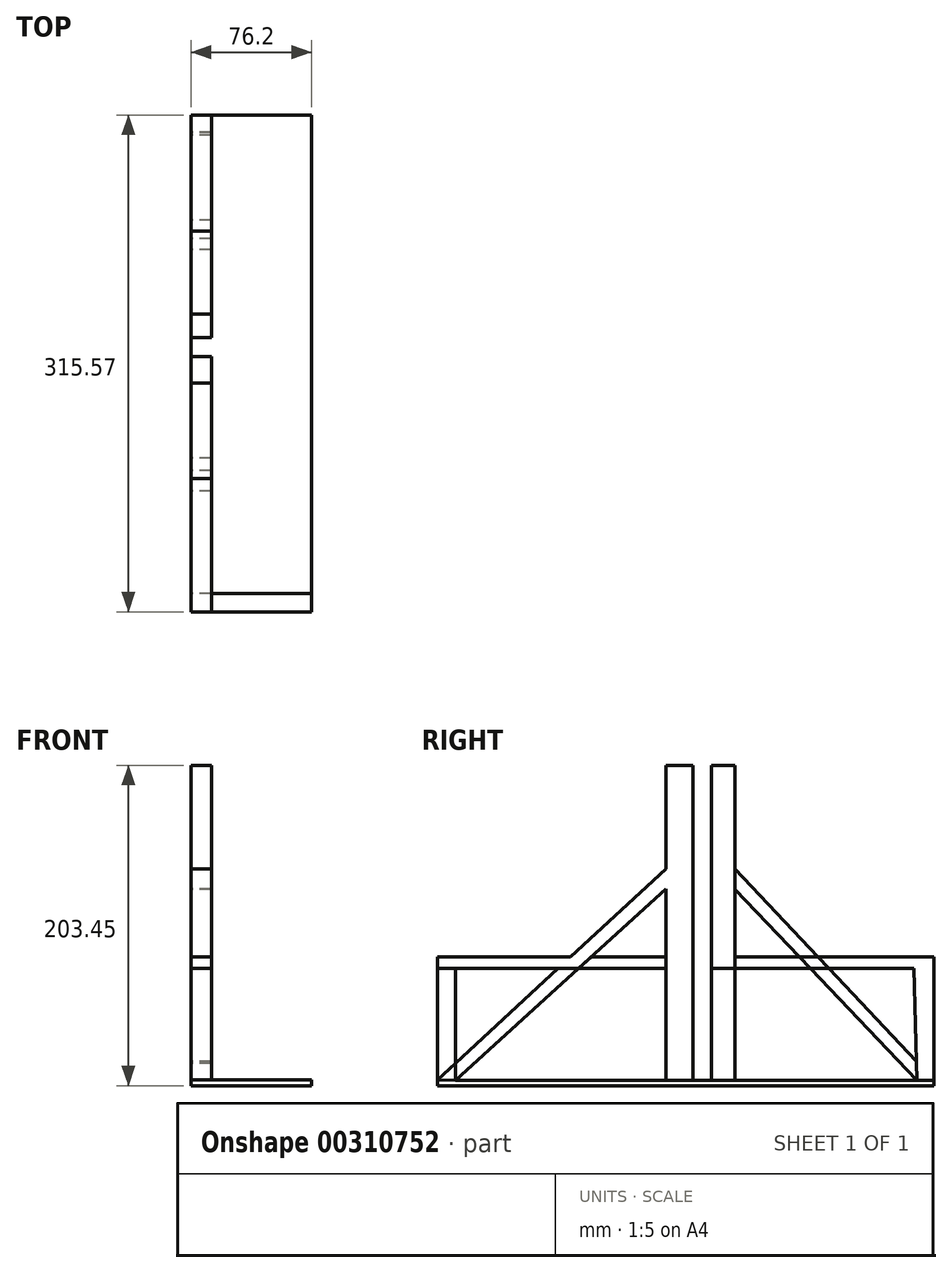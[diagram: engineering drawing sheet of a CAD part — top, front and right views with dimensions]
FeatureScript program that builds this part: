
annotation { "Feature Type Name" : "Feature", "Feature Type Description" : "" }
export const myFeature = defineFeature(function(context is Context, id is Id, definition is map)
    precondition{}
    {
        {
            var Q0;
            Q0=qCreatedBy(makeId("Right.planeOp"),FACE);
            var sketch = newSketch(context, id + "F0", { "sketchPlane" : qUnion([Q0])});
            skLineSegment(sketch, "E0.bottom", {"start": v(178.4, 15.69) * mm, "end": v(-125.56, 15.69) * mm});
            skLineSegment(sketch, "E0.top", {"start": v(178.4, -55.38) * mm, "end": v(-125.56, -55.38) * mm});
            skLineSegment(sketch, "E0.left", {"start": v(178.4, 15.69) * mm, "end": v(178.4, -55.38) * mm});
            skLineSegment(sketch, "E0.right", {"start": v(-125.56, 15.69) * mm, "end": v(-125.56, -55.38) * mm});
            skLineSegment(sketch, "E1", {"start": v(51.97, -55.38) * mm, "end": v(51.97, 144.7) * mm});
            skLineSegment(sketch, "E2", {"start": v(8.17, -55.38) * mm, "end": v(8.17, 144.7) * mm});
            skLineSegment(sketch, "E3", {"start": v(51.97, 144.7) * mm, "end": v(37.04, 144.7) * mm});
            skLineSegment(sketch, "E4", {"start": v(37.04, 144.7) * mm, "end": v(37.04, -55.38) * mm});
            skLineSegment(sketch, "E5", {"start": v(8.17, 144.7) * mm, "end": v(25.1, 144.7) * mm});
            skLineSegment(sketch, "E6", {"start": v(25.1, 144.7) * mm, "end": v(25.1, -55.38) * mm});
            skLineSegment(sketch, "E7", {"start": v(51.97, 79) * mm, "end": v(178.4, -55.38) * mm});
            skLineSegment(sketch, "E8", {"start": v(51.97, 66.06) * mm, "end": v(167.44, -55.38) * mm});
            skLineSegment(sketch, "E9", {"start": v(-125.56, 15.69) * mm, "end": v(-137.17, 15.69) * mm});
            skLineSegment(sketch, "E10", {"start": v(-137.17, 15.69) * mm, "end": v(-137.17, -55.2) * mm});
            skLineSegment(sketch, "E11", {"start": v(-137.17, -55.2) * mm, "end": v(-125.56, -55.38) * mm});
            skLineSegment(sketch, "E12", {"start": v(-137.17, 15.69) * mm, "end": v(-137.17, 22.96) * mm});
            skLineSegment(sketch, "E13", {"start": v(-137.17, 22.96) * mm, "end": v(8.17, 22.96) * mm});
            skLineSegment(sketch, "E14", {"start": v(51.97, 22.96) * mm, "end": v(178.4, 22.96) * mm});
            skLineSegment(sketch, "E15", {"start": v(178.4, 22.96) * mm, "end": v(178.4, 15.69) * mm});
            skLineSegment(sketch, "E16", {"start": v(8.17, 66.1) * mm, "end": v(-125.56, -55.38) * mm});
            skLineSegment(sketch, "E17", {"start": v(8.17, 79) * mm, "end": v(-137.17, -55.2) * mm});
            skLineSegment(sketch, "E18", {"start": v(165.56, 15.69) * mm, "end": v(167.44, -55.38) * mm});
            skLineSegment(sketch, "E19", {"start": v(178.4, -55.38) * mm, "end": v(178.4, -58.74) * mm});
            skLineSegment(sketch, "E20", {"start": v(178.4, -58.74) * mm, "end": v(-137.17, -58.74) * mm});
            skLineSegment(sketch, "E21", {"start": v(-137.17, -55.2) * mm, "end": v(-137.17, -58.74) * mm});
            skSolve(sketch);
        }
        {
            var Q0;
            {var subQ0=sQuery(id+"F0.wireOp",EDGE,"E0.left");Q0=makeQuery(id+"F0.imprint","IMPRINT",FACE,{"disambiguationData":[TD([[makeQuery(id+"F0.imprint","IMPRINT",EDGE,{"derivedFrom":subQ0}),-1.0]])]});}
            var Q1;
            {var subQ0=sQuery(id+"F0.wireOp",EDGE,"E7");var subQ3=sQuery(id+"F0.wireOp",EDGE,"E18");var subQ5=makeQuery(id+"F0.imprint","INTERSECT",VERTEX,{"derivedFrom":[subQ0,subQ3]});Q1=makeQuery(id+"F0.imprint","IMPRINT",FACE,{"disambiguationData":[TD([[makeQuery(id+"F0.imprint","IMPRINT",EDGE,{"disambiguationData":[TD([[subQ5,-1.0]])],"derivedFrom":subQ3}),1.0]])]});}
            var Q2;
            {var subQ0=sQuery(id+"F0.wireOp",EDGE,"E15");Q2=makeQuery(id+"F0.imprint","IMPRINT",FACE,{"disambiguationData":[TD([[makeQuery(id+"F0.imprint","IMPRINT",EDGE,{"derivedFrom":subQ0}),-1.0]])]});}
            var Q3;
            {var subQ0=sQuery(id+"F0.wireOp",EDGE,"E8");var subQ1=sQuery(id+"F0.wireOp",EDGE,"E0.bottom");var subQ2=makeQuery(id+"F0.imprint","INTERSECT",VERTEX,{"derivedFrom":[subQ1,subQ0]});Q3=makeQuery(id+"F0.imprint","IMPRINT",FACE,{"disambiguationData":[TD([[makeQuery(id+"F0.imprint","IMPRINT",EDGE,{"disambiguationData":[TD([[subQ2,-1.0]])],"derivedFrom":subQ1}),-1.0]])]});}
            var Q4;
            {var subQ0=sQuery(id+"F0.wireOp",EDGE,"E7");var subQ1=sQuery(id+"F0.wireOp",EDGE,"E1");var subQ2=makeQuery(id+"F0.imprint","INTERSECT",VERTEX,{"derivedFrom":[subQ1,subQ0]});Q4=makeQuery(id+"F0.imprint","IMPRINT",FACE,{"disambiguationData":[TD([[makeQuery(id+"F0.imprint","IMPRINT",EDGE,{"disambiguationData":[TD([[subQ2,1.0]])],"derivedFrom":subQ1}),-1.0]])]});}
            var Q5;
            {var subQ0=sQuery(id+"F0.wireOp",EDGE,"E4");var subQ1=sQuery(id+"F0.wireOp",EDGE,"E0.bottom");var subQ2=makeQuery(id+"F0.imprint","INTERSECT",VERTEX,{"derivedFrom":[subQ1,subQ0]});Q5=makeQuery(id+"F0.imprint","IMPRINT",FACE,{"disambiguationData":[TD([[makeQuery(id+"F0.imprint","IMPRINT",EDGE,{"disambiguationData":[TD([[subQ2,1.0]])],"derivedFrom":subQ1}),1.0]])]});}
            var Q6;
            {var subQ0=sQuery(id+"F0.wireOp",EDGE,"E6");var subQ1=sQuery(id+"F0.wireOp",EDGE,"E0.bottom");var subQ2=makeQuery(id+"F0.imprint","INTERSECT",VERTEX,{"derivedFrom":[subQ1,subQ0]});Q6=makeQuery(id+"F0.imprint","IMPRINT",FACE,{"disambiguationData":[TD([[makeQuery(id+"F0.imprint","IMPRINT",EDGE,{"disambiguationData":[TD([[subQ2,-1.0]])],"derivedFrom":subQ1}),1.0]])]});}
            var Q7;
            {var subQ8=sQuery(id+"F0.wireOp",EDGE,"E5");Q7=makeQuery(id+"F0.imprint","IMPRINT",FACE,{"disambiguationData":[TD([[makeQuery(id+"F0.imprint","IMPRINT",EDGE,{"derivedFrom":subQ8}),-1.0]])]});}
            var Q8;
            {var subQ0=sQuery(id+"F0.wireOp",EDGE,"E16");var subQ1=sQuery(id+"F0.wireOp",EDGE,"E2");var subQ2=makeQuery(id+"F0.imprint","INTERSECT",VERTEX,{"derivedFrom":[subQ1,subQ0]});Q8=makeQuery(id+"F0.imprint","IMPRINT",FACE,{"disambiguationData":[TD([[makeQuery(id+"F0.imprint","IMPRINT",EDGE,{"disambiguationData":[TD([[subQ2,-1.0]])],"derivedFrom":subQ1}),1.0]])]});}
            var Q9;
            {var subQ0=sQuery(id+"F0.wireOp",EDGE,"E16");var subQ1=sQuery(id+"F0.wireOp",EDGE,"E0.bottom");var subQ2=makeQuery(id+"F0.imprint","INTERSECT",VERTEX,{"derivedFrom":[subQ1,subQ0]});Q9=makeQuery(id+"F0.imprint","IMPRINT",FACE,{"disambiguationData":[TD([[makeQuery(id+"F0.imprint","IMPRINT",EDGE,{"disambiguationData":[TD([[subQ2,-1.0]])],"derivedFrom":subQ1}),-1.0]])]});}
            var Q10;
            {var subQ6=sQuery(id+"F0.wireOp",EDGE,"E9");Q10=makeQuery(id+"F0.imprint","IMPRINT",FACE,{"disambiguationData":[TD([[makeQuery(id+"F0.imprint","IMPRINT",EDGE,{"derivedFrom":subQ6}),-1.0]])]});}
            var Q11;
            {var subQ0=sQuery(id+"F0.wireOp",EDGE,"E7");var subQ1=sQuery(id+"F0.wireOp",EDGE,"E0.bottom");var subQ2=makeQuery(id+"F0.imprint","INTERSECT",VERTEX,{"derivedFrom":[subQ1,subQ0]});Q11=makeQuery(id+"F0.imprint","IMPRINT",FACE,{"disambiguationData":[TD([[makeQuery(id+"F0.imprint","IMPRINT",EDGE,{"disambiguationData":[TD([[subQ2,-1.0]])],"derivedFrom":subQ1}),-1.0]])]});}
            extrude(context, id + "F1", {"entities" : qUnion([Q0, Q1, Q2, Q3, Q4, Q5, Q6, Q7, Q8, Q9, Q10, Q11]), "depth" : 12.7 * mm});
        }
        {
            var Q0;
            {var subQ8=sQuery(id+"F0.wireOp",EDGE,"E3");Q0=makeQuery(id+"F0.imprint","IMPRINT",FACE,{"disambiguationData":[TD([[makeQuery(id+"F0.imprint","IMPRINT",EDGE,{"derivedFrom":subQ8}),1.0]])]});}
            var Q1;
            {var subQ0=sQuery(id+"F0.wireOp",EDGE,"E7");var subQ1=sQuery(id+"F0.wireOp",EDGE,"E0.bottom");var subQ2=makeQuery(id+"F0.imprint","INTERSECT",VERTEX,{"derivedFrom":[subQ1,subQ0]});Q1=makeQuery(id+"F0.imprint","IMPRINT",FACE,{"disambiguationData":[TD([[makeQuery(id+"F0.imprint","IMPRINT",EDGE,{"disambiguationData":[TD([[subQ2,-1.0]])],"derivedFrom":subQ1}),1.0]])]});}
            var Q2;
            {var subQ0=sQuery(id+"F0.wireOp",EDGE,"E2");var subQ1=sQuery(id+"F0.wireOp",EDGE,"E0.bottom");var subQ2=makeQuery(id+"F0.imprint","INTERSECT",VERTEX,{"derivedFrom":[subQ1,subQ0]});Q2=makeQuery(id+"F0.imprint","IMPRINT",FACE,{"disambiguationData":[TD([[makeQuery(id+"F0.imprint","IMPRINT",EDGE,{"disambiguationData":[TD([[subQ2,-1.0]])],"derivedFrom":subQ1}),-1.0]])]});}
            var Q3;
            {var subQ0=sQuery(id+"F0.wireOp",EDGE,"E16");var subQ1=sQuery(id+"F0.wireOp",EDGE,"E0.bottom");var subQ2=makeQuery(id+"F0.imprint","INTERSECT",VERTEX,{"derivedFrom":[subQ1,subQ0]});Q3=makeQuery(id+"F0.imprint","IMPRINT",FACE,{"disambiguationData":[TD([[makeQuery(id+"F0.imprint","IMPRINT",EDGE,{"disambiguationData":[TD([[subQ2,-1.0]])],"derivedFrom":subQ1}),1.0]])]});}
            var Q4;
            {var subQ0=sQuery(id+"F0.wireOp",EDGE,"E9");Q4=makeQuery(id+"F0.imprint","IMPRINT",FACE,{"disambiguationData":[TD([[makeQuery(id+"F0.imprint","IMPRINT",EDGE,{"derivedFrom":subQ0}),1.0]])]});}
            extrude(context, id + "F2", {"entities" : qUnion([Q0, Q1, Q2, Q3, Q4]), "depth" : 12.7 * mm});
        }
        {
            var Q0;
            {var subQ0=sQuery(id+"F0.wireOp",EDGE,"E7");var subQ1=sQuery(id+"F0.wireOp",EDGE,"E0.bottom");var subQ2=makeQuery(id+"F0.imprint","INTERSECT",VERTEX,{"derivedFrom":[subQ1,subQ0]});Q0=makeQuery(id+"F0.imprint","IMPRINT",FACE,{"disambiguationData":[TD([[makeQuery(id+"F0.imprint","IMPRINT",EDGE,{"disambiguationData":[TD([[subQ2,-1.0]])],"derivedFrom":subQ1}),-1.0]])]});}
            extrude(context, id + "F3", {"entities" : qUnion([Q0]), "depth" : 12.7 * mm});
        }
        {
            var Q0;
            {var subQ0=sQuery(id+"F0.wireOp",EDGE,"E11");Q0=makeQuery(id+"F0.imprint","IMPRINT",FACE,{"disambiguationData":[TD([[makeQuery(id+"F0.imprint","IMPRINT",EDGE,{"derivedFrom":subQ0}),1.0]])]});}
            extrude(context, id + "F4", {"entities" : qUnion([Q0]), "depth" : 12.7 * mm});
        }
        {
            var Q0;
            {var subQ5=sQuery(id+"F0.wireOp",EDGE,"E11");Q0=makeQuery(id+"F0.imprint","IMPRINT",FACE,{"disambiguationData":[TD([[makeQuery(id+"F0.imprint","IMPRINT",EDGE,{"derivedFrom":subQ5}),-1.0]])]});}
            extrude(context, id + "F5", {"entities" : qUnion([Q0]), "depth" : 76.2 * mm});
        }
    });
